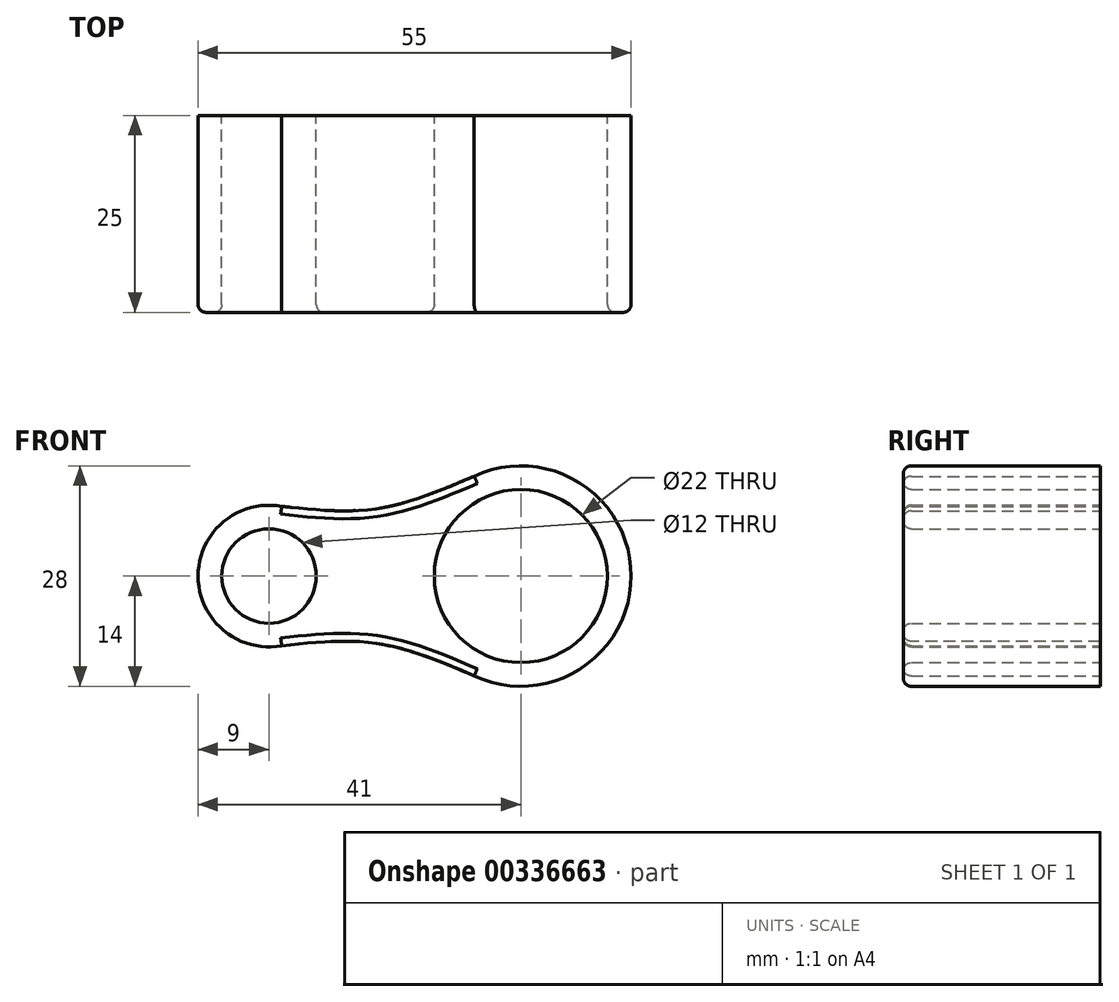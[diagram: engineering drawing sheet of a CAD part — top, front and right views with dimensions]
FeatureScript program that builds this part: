
annotation { "Feature Type Name" : "Feature", "Feature Type Description" : "" }
export const myFeature = defineFeature(function(context is Context, id is Id, definition is map)
    precondition{}
    {
        {
            var Q0;
            Q0=qCreatedBy(makeId("Front.planeOp"),FACE);
            var sketch = newSketch(context, id + "F0", { "sketchPlane" : qUnion([Q0])});
            skCircle(sketch, "E0", {"center": v(0, 0) * mm, "radius": 14 * mm});
            skCircle(sketch, "E1", {"center": v(0, 0) * mm, "radius": 11 * mm});
            skCircle(sketch, "E2", {"center": v(-32, 0) * mm, "radius": 9 * mm});
            skCircle(sketch, "E3", {"center": v(-32, 0) * mm, "radius": 6 * mm});
            skFitSpline(sketch, "E4", {"points": [v(-30.38, 8.85) * mm, v(-18.21, 8.58) * mm, v(-5.93, 12.68) * mm], "startDerivative": vector(24.84, -2.68) * mm, "endDerivative": vector(24.05, 10.27) * mm});
            skLineSegment(sketch, "E5", {"start": v(-32, 0) * mm, "end": v(0, 0) * mm});
            skFitSpline(sketch, "E6.MirrorCS", {"points": [v(-30.38, -8.85) * mm, v(-18.21, -8.58) * mm, v(-5.93, -12.68) * mm], "startDerivative": vector(24.84, 2.68) * mm, "endDerivative": vector(24.05, -10.27) * mm});
            skSolve(sketch);
        }
        {
            var Q0;
            Q0=qSketchRegion(id+"F0",true);
            extrude(context, id + "F1", {"entities" : qUnion([Q0]), "depth" : 25 * mm});
        }
        {
            var Q0;
            Q0=makeQuery(id+"F1.opExtrude","CAP_EDGE",EDGE,{"disambiguationData":[OSD([sQuery(id+"F0.wireOp",EDGE,"E1")])],"isStart":false});
            var Q1;
            Q1=makeQuery(id+"F1.opExtrude","CAP_EDGE",EDGE,{"disambiguationData":[OSD([sQuery(id+"F0.wireOp",EDGE,"E3")])],"isStart":false});
            var Q2;
            Q2=makeQuery(id+"F1.opExtrude","CAP_EDGE",EDGE,{"disambiguationData":[OSD([sQuery(id+"F0.wireOp",EDGE,"E2")])],"isStart":false});
            var Q3;
            Q3=makeQuery(id+"F1.opExtrude","CAP_EDGE",EDGE,{"disambiguationData":[OSD([sQuery(id+"F0.wireOp",EDGE,"E0")])],"isStart":false});
            fillet(context, id + "F2", {"entities" : qUnion([Q0, Q1, Q2, Q3]), "radius" : 1 * mm, "tangentPropagation" : true, "allowEdgeOverflow" : false});
        }
    });
